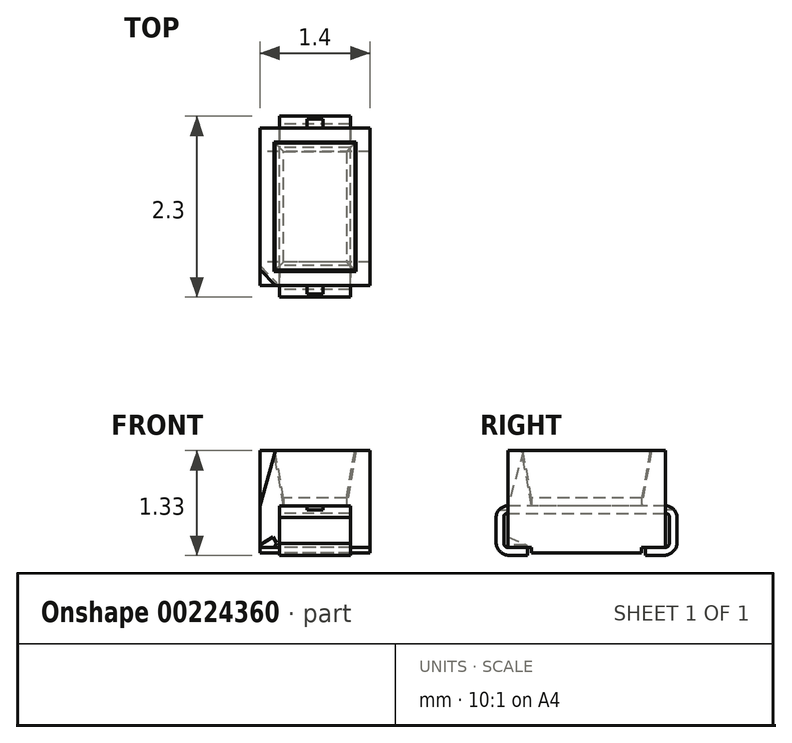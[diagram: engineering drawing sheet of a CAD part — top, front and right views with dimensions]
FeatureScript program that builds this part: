
annotation { "Feature Type Name" : "Feature", "Feature Type Description" : "" }
export const myFeature = defineFeature(function(context is Context, id is Id, definition is map)
    precondition{}
    {
        {
            var Q0;
            Q0=qCreatedBy(makeId("Top.planeOp"),FACE);
            var sketch = newSketch(context, id + "F0", { "sketchPlane" : qUnion([Q0])});
            skLineSegment(sketch, "E0.bottom", {"start": v(0.7, -1) * mm, "end": v(-0.7, -1) * mm});
            skLineSegment(sketch, "E0.top", {"start": v(0.7, 1) * mm, "end": v(-0.7, 1) * mm});
            skLineSegment(sketch, "E0.left", {"start": v(0.7, -1) * mm, "end": v(0.7, 1) * mm});
            skLineSegment(sketch, "E0.right", {"start": v(-0.7, -1) * mm, "end": v(-0.7, 1) * mm});
            skPoint(sketch, "E0.middle", {"position": v(0, 0) * mm});
            skLineSegment(sketch, "E1.bottom", {"start": v(0.4, -0.7) * mm, "end": v(-0.4, -0.7) * mm});
            skLineSegment(sketch, "E1.top", {"start": v(0.4, 0.7) * mm, "end": v(-0.4, 0.7) * mm});
            skLineSegment(sketch, "E1.left", {"start": v(0.4, -0.7) * mm, "end": v(0.4, 0.7) * mm});
            skLineSegment(sketch, "E1.right", {"start": v(-0.4, -0.7) * mm, "end": v(-0.4, 0.7) * mm});
            skLineSegment(sketch, "E2.bottom", {"start": v(0.15, -0.4) * mm, "end": v(-0.15, -0.4) * mm});
            skLineSegment(sketch, "E2.top", {"start": v(0.15, -0.1) * mm, "end": v(-0.15, -0.1) * mm});
            skLineSegment(sketch, "E2.left", {"start": v(0.15, -0.4) * mm, "end": v(0.15, -0.1) * mm});
            skLineSegment(sketch, "E2.right", {"start": v(-0.15, -0.4) * mm, "end": v(-0.15, -0.1) * mm});
            skPoint(sketch, "E2.middle", {"position": v(0, -0.25) * mm});
            skSolve(sketch);
        }
        {
            var Q0;
            Q0=makeQuery(id+"F0.imprint","IMPRINT",FACE,{"disambiguationData":[TD([[makeQuery(id+"F0.imprint","IMPRINT",EDGE,{"derivedFrom":sQuery(id+"F0.wireOp",EDGE,"E0.bottom")}),-1.0]])]});
            var Q1;
            {var subQ1=sQuery(id+"F0.wireOp",EDGE,"E0.top");Q1=makeQuery(id+"F0.imprint","IMPRINT",FACE,{"disambiguationData":[TD([[makeQuery(id+"F0.imprint","IMPRINT",EDGE,{"derivedFrom":subQ1}),1.0]])]});}
            extrude(context, id + "F1", {"entities" : qUnion([Q0, Q1]), "depth" : .7 * mm, "hasSecondDirection" : true, "secondDirectionOppositeDirection" : true, "secondDirectionDepth" : .6 * mm});
        }
        {
            var Q0;
            Q0=makeQuery(id+"F0.imprint","IMPRINT",FACE,{"disambiguationData":[TD([[makeQuery(id+"F0.imprint","IMPRINT",EDGE,{"derivedFrom":sQuery(id+"F0.wireOp",EDGE,"E1.bottom")}),-1.0]])]});
            var Q1;
            Q1=makeQuery(id+"F1.opExtrude","CAP_FACE",FACE,{"disambiguationData":[OSD([sQuery(id+"F0.wireOp",EDGE,"E0.bottom"),sQuery(id+"F0.wireOp",EDGE,"E0.top"),sQuery(id+"F0.wireOp",EDGE,"E0.left"),sQuery(id+"F0.wireOp",EDGE,"E0.right"),sQuery(id+"F0.wireOp",EDGE,"E1.bottom"),sQuery(id+"F0.wireOp",EDGE,"E1.top"),sQuery(id+"F0.wireOp",EDGE,"E1.left"),sQuery(id+"F0.wireOp",EDGE,"E1.right")])],"isStart":false});
            extrude(context, id + "F2", {"entities" : qUnion([Q0]), "operationType" : NewBodyOperationType.REMOVE, "endBound" : BoundingType.UP_TO_SURFACE, "endBoundEntityFace" : qUnion([Q1]), "depth" : 25 * mm, "hasDraft" : true, "draftAngle" : 10 * degree});
        }
        {
            var Q0;
            Q0=makeQuery(id+"F0.imprint","IMPRINT",FACE,{"disambiguationData":[TD([[makeQuery(id+"F0.imprint","IMPRINT",EDGE,{"derivedFrom":sQuery(id+"F0.wireOp",EDGE,"E2.bottom")}),-1.0]])]});
            extrude(context, id + "F3", {"entities" : qUnion([Q0]), "depth" : .1 * mm});
        }
        {
            var Q0;
            Q0=makeQuery(id+"F0.imprint","IMPRINT",FACE,{"disambiguationData":[TD([[makeQuery(id+"F0.imprint","IMPRINT",EDGE,{"derivedFrom":sQuery(id+"F0.wireOp",EDGE,"E1.bottom")}),-1.0]])]});
            var Q1;
            Q1=makeQuery(id+"F1.opExtrude","CAP_FACE",FACE,{"disambiguationData":[OSD([sQuery(id+"F0.wireOp",EDGE,"E0.bottom"),sQuery(id+"F0.wireOp",EDGE,"E0.top"),sQuery(id+"F0.wireOp",EDGE,"E0.left"),sQuery(id+"F0.wireOp",EDGE,"E0.right"),sQuery(id+"F0.wireOp",EDGE,"E1.bottom"),sQuery(id+"F0.wireOp",EDGE,"E1.top"),sQuery(id+"F0.wireOp",EDGE,"E1.left"),sQuery(id+"F0.wireOp",EDGE,"E1.right")])],"isStart":true});
            extrude(context, id + "F4", {"entities" : qUnion([Q0]), "operationType" : NewBodyOperationType.ADD, "endBound" : BoundingType.UP_TO_SURFACE, "oppositeDirection" : true, "endBoundEntityFace" : qUnion([Q1]), "depth" : 25 * mm});
        }
        {
            var Q0;
            Q0=makeQuery(id+"F0.imprint","IMPRINT",FACE,{"disambiguationData":[TD([[makeQuery(id+"F0.imprint","IMPRINT",EDGE,{"derivedFrom":sQuery(id+"F0.wireOp",EDGE,"E1.bottom")}),-1.0]])]});
            extrude(context, id + "F5", {"entities" : qUnion([Q0]), "depth" : .1 * mm});
        }
        {
            var Q0;
            Q0=makeQuery(id+"F0.imprint","IMPRINT",FACE,{"disambiguationData":[TD([[makeQuery(id+"F0.imprint","IMPRINT",EDGE,{"derivedFrom":sQuery(id+"F0.wireOp",EDGE,"E2.bottom")}),-1.0]])]});
            var Q1;
            {var subQ0=sQuery(id+"F0.wireOp",EDGE,"E1.right");var subQ1=sQuery(id+"F0.wireOp",EDGE,"E1.left");var subQ2=sQuery(id+"F0.wireOp",EDGE,"E1.top");var subQ3=sQuery(id+"F0.wireOp",EDGE,"E1.bottom");var subQ4=sQuery(id+"F0.wireOp",EDGE,"E0.right");var subQ5=sQuery(id+"F0.wireOp",EDGE,"E0.left");var subQ6=sQuery(id+"F0.wireOp",EDGE,"E0.top");var subQ7=sQuery(id+"F0.wireOp",EDGE,"E0.bottom");Q1=makeQuery(id+"F4.boolean.opBoolean","MERGE",FACE,{"derivedFrom":[makeQuery(id+"F1.opExtrude","CAP_FACE",FACE,{"disambiguationData":[OSD([subQ7,subQ6,subQ5,subQ4,subQ3,subQ2,subQ1,subQ0])],"isStart":true}),makeQuery(id+"F4.opExtrude","CAP_FACE",FACE,{"disambiguationData":[OSD([subQ7,subQ6,subQ5,subQ4,subQ3,subQ2,subQ1,subQ0])],"isStart":false})]});}
            extrude(context, id + "F6", {"entities" : qUnion([Q0]), "operationType" : NewBodyOperationType.ADD, "endBound" : BoundingType.UP_TO_SURFACE, "oppositeDirection" : true, "endBoundEntityFace" : qUnion([Q1]), "depth" : 25 * mm});
        }
        {
            var Q0;
            Q0=makeQuery(id+"F1.opExtrude","SWEPT_FACE",FACE,{"disambiguationData":[OSD([sQuery(id+"F0.wireOp",EDGE,"E0.right")])]});
            var sketch = newSketch(context, id + "F7", { "sketchPlane" : qUnion([Q0])});
            skLineSegment(sketch, "E3", {"start": v(-1, 0.7) * mm, "end": v(1, 0.7) * mm, "construction": true});
            skLineSegment(sketch, "E4", {"start": v(1, 0.7) * mm, "end": v(1, -0.6) * mm, "construction": true});
            skLineSegment(sketch, "E5", {"start": v(1, -0.6) * mm, "end": v(-1, -0.6) * mm, "construction": true});
            skLineSegment(sketch, "E6", {"start": v(-1, -0.6) * mm, "end": v(-1, 0.7) * mm, "construction": true});
            skLineSegment(sketch, "E7", {"start": v(-1.16, -0.53) * mm, "end": v(-0.7, -0.53) * mm});
            skLineSegment(sketch, "E8", {"start": v(-0.7, -0.53) * mm, "end": v(-0.7, -0.74) * mm});
            skLineSegment(sketch, "E9", {"start": v(-0.7, -0.74) * mm, "end": v(0.7, -0.74) * mm});
            skLineSegment(sketch, "E10", {"start": v(0.7, -0.74) * mm, "end": v(0.7, -0.53) * mm});
            skLineSegment(sketch, "E11", {"start": v(0.7, -0.53) * mm, "end": v(1.16, -0.53) * mm});
            skLineSegment(sketch, "E12", {"start": v(1.16, -0.53) * mm, "end": v(1.16, -0.97) * mm});
            skLineSegment(sketch, "E13", {"start": v(1.16, -0.97) * mm, "end": v(-1.16, -0.97) * mm});
            skLineSegment(sketch, "E14", {"start": v(-1.16, -0.97) * mm, "end": v(-1.16, -0.53) * mm});
            skSolve(sketch);
        }
        {
            var Q0;
            {var subQ0=sQuery(id+"F7.wireOp",EDGE,"E8");var subQ1=sQuery(id+"F7.wireOp",EDGE,"E7");var subQ2=makeQuery(id+"F7.imprint","INTERSECT",VERTEX,{"derivedFrom":[subQ1,subQ0]});Q0=makeQuery(id+"F7.imprint","IMPRINT",FACE,{"disambiguationData":[TD([[makeQuery(id+"F7.imprint","IMPRINT",EDGE,{"disambiguationData":[TD([[subQ2,-1.0]])],"derivedFrom":subQ0}),-1.0]])]});}
            var Q1;
            {var subQ0=sQuery(id+"F7.wireOp",EDGE,"E11");var subQ1=sQuery(id+"F7.wireOp",EDGE,"E10");var subQ2=makeQuery(id+"F7.imprint","INTERSECT",VERTEX,{"derivedFrom":[subQ1,subQ0]});Q1=makeQuery(id+"F7.imprint","IMPRINT",FACE,{"disambiguationData":[TD([[makeQuery(id+"F7.imprint","IMPRINT",EDGE,{"disambiguationData":[TD([[subQ2,1.0]])],"derivedFrom":subQ1}),-1.0]])]});}
            extrude(context, id + "F8", {"entities" : qUnion([Q0, Q1]), "operationType" : NewBodyOperationType.REMOVE, "endBound" : BoundingType.UP_TO_NEXT, "oppositeDirection" : true, "depth" : 25 * mm});
        }
        {
            var Q0;
            Q0=makeQuery(id+"F1.opExtrude","SWEPT_FACE",FACE,{"disambiguationData":[OSD([sQuery(id+"F0.wireOp",EDGE,"E0.right")])]});
            var sketch = newSketch(context, id + "F9", { "sketchPlane" : qUnion([Q0])});
            skLineSegment(sketch, "E15", {"start": v(-1, 0) * mm, "end": v(1, 0) * mm, "construction": true});
            skLineSegment(sketch, "E16", {"start": v(-1.15, -0.15) * mm, "end": v(-1.15, -0.48) * mm});
            skLineSegment(sketch, "E17", {"start": v(-1, -0.63) * mm, "end": v(-0.75, -0.63) * mm});
            skLineSegment(sketch, "E18", {"start": v(-1.15, 0) * mm, "end": v(1.15, 0) * mm});
            skLineSegment(sketch, "E19", {"start": v(1.15, -0.15) * mm, "end": v(1.15, -0.48) * mm});
            skLineSegment(sketch, "E20", {"start": v(1, -0.63) * mm, "end": v(0.75, -0.63) * mm});
            skLineSegment(sketch, "E21", {"start": v(0.75, -0.63) * mm, "end": v(0.75, -0.53) * mm});
            skLineSegment(sketch, "E22", {"start": v(0.75, -0.53) * mm, "end": v(1, -0.53) * mm});
            skLineSegment(sketch, "E23", {"start": v(1.05, -0.48) * mm, "end": v(1.05, -0.15) * mm});
            skLineSegment(sketch, "E24", {"start": v(1, -0.1) * mm, "end": v(-1, -0.1) * mm});
            skLineSegment(sketch, "E25", {"start": v(-1.05, -0.15) * mm, "end": v(-1.05, -0.48) * mm});
            skLineSegment(sketch, "E26", {"start": v(-1, -0.53) * mm, "end": v(-0.75, -0.53) * mm});
            skLineSegment(sketch, "E27", {"start": v(-0.75, -0.53) * mm, "end": v(-0.75, -0.63) * mm});
            skPoint(sketch, "E28.visualSharp", {"position": v(-1.05, -0.1) * mm});
            skArc(sketch, "E28.filletArc", {"start": v(-1, -0.1) * mm, "mid": v(-1.04, -0.11) * mm, "end": v(-1.05, -0.15) * mm});
            skPoint(sketch, "E29.newPointA", {"position": v(0, 0) * mm});
            skArc(sketch, "E29.filletArc", {"start": v(-1, 0) * mm, "mid": v(-1.1, -0.04) * mm, "end": v(-1.15, -0.15) * mm});
            skPoint(sketch, "E30.visualSharp", {"position": v(-1.15, -0.63) * mm});
            skArc(sketch, "E30.filletArc", {"start": v(-1.15, -0.48) * mm, "mid": v(-1.1, -0.58) * mm, "end": v(-1, -0.63) * mm});
            skPoint(sketch, "E31.visualSharp", {"position": v(-1.05, -0.53) * mm});
            skArc(sketch, "E31.filletArc", {"start": v(-1.05, -0.48) * mm, "mid": v(-1.04, -0.51) * mm, "end": v(-1, -0.53) * mm});
            skPoint(sketch, "E32.visualSharp", {"position": v(1.05, -0.53) * mm});
            skArc(sketch, "E32.filletArc", {"start": v(1, -0.53) * mm, "mid": v(1.04, -0.51) * mm, "end": v(1.05, -0.48) * mm});
            skPoint(sketch, "E33.visualSharp", {"position": v(1.05, -0.1) * mm});
            skArc(sketch, "E33.filletArc", {"start": v(1.05, -0.15) * mm, "mid": v(1.04, -0.11) * mm, "end": v(1, -0.1) * mm});
            skArc(sketch, "E34.filletArc", {"start": v(1.15, -0.15) * mm, "mid": v(1.1, -0.04) * mm, "end": v(1, 0) * mm});
            skPoint(sketch, "E35.visualSharp", {"position": v(1.15, -0.63) * mm});
            skArc(sketch, "E35.filletArc", {"start": v(1, -0.63) * mm, "mid": v(1.1, -0.58) * mm, "end": v(1.15, -0.48) * mm});
            skSolve(sketch);
        }
        {
            var Q0;
            Q0=qSketchRegion(id+"F9",true);
            var Q1;
            Q1=makeQuery(id+"F1.opExtrude","SWEPT_FACE",FACE,{"disambiguationData":[OSD([sQuery(id+"F0.wireOp",EDGE,"E0.left")])]});
            extrude(context, id + "F10", {"entities" : qUnion([Q0]), "oppositeDirection" : true, "endBoundEntityFace" : qUnion([Q1]), "depth" : 1.15 * mm, "hasSecondDirection" : true, "secondDirectionOppositeDirection" : true, "secondDirectionDepth" : .25 * mm});
        }
        {
            var Q0;
            Q0=makeQuery(id+"F5.opExtrude","CAP_FACE",FACE,{"disambiguationData":[OSD([sQuery(id+"F0.wireOp",EDGE,"E1.bottom"),sQuery(id+"F0.wireOp",EDGE,"E1.top"),sQuery(id+"F0.wireOp",EDGE,"E1.left"),sQuery(id+"F0.wireOp",EDGE,"E1.right"),sQuery(id+"F0.wireOp",EDGE,"E2.bottom"),sQuery(id+"F0.wireOp",EDGE,"E2.top"),sQuery(id+"F0.wireOp",EDGE,"E2.left"),sQuery(id+"F0.wireOp",EDGE,"E2.right")])],"isStart":false});
            var sketch = newSketch(context, id + "F11", { "sketchPlane" : qUnion([Q0])});
            skLineSegment(sketch, "E36.0.1", {"start": v(-0.45, 1) * mm, "end": v(0.45, 1) * mm});
            skLineSegment(sketch, "E37", {"start": v(0, 1) * mm, "end": v(0.1, 1) * mm});
            skLineSegment(sketch, "E38", {"start": v(0.1, 1) * mm, "end": v(0.1, 1.2) * mm});
            skLineSegment(sketch, "E39", {"start": v(0.1, 1.2) * mm, "end": v(-0.1, 1.2) * mm});
            skLineSegment(sketch, "E40", {"start": v(-0.1, 1.2) * mm, "end": v(-0.1, 1) * mm});
            skLineSegment(sketch, "E41", {"start": v(-0.1, 1) * mm, "end": v(0, 1) * mm});
            skPoint(sketch, "E42.startSnap0", {"position": v(-0.15, -0.25) * mm});
            skPoint(sketch, "E36.0.2.end.orphan", {"position": v(0.45, 1.15) * mm});
            skPoint(sketch, "E36.0.0.start.orphan", {"position": v(-0.45, 1.15) * mm});
            skLineSegment(sketch, "E43", {"start": v(-0.78, 0) * mm, "end": v(1.2, 0) * mm, "construction": true});
            skLineSegment(sketch, "E44.MirrorCS", {"start": v(-0.1, -1) * mm, "end": v(0, -1) * mm});
            skLineSegment(sketch, "E45.MirrorCS", {"start": v(-0.1, -1.2) * mm, "end": v(-0.1, -1) * mm});
            skLineSegment(sketch, "E46.MirrorCS", {"start": v(0, -1) * mm, "end": v(0.1, -1) * mm});
            skLineSegment(sketch, "E47.MirrorCS", {"start": v(0.1, -1.2) * mm, "end": v(-0.1, -1.2) * mm});
            skLineSegment(sketch, "E48.MirrorCS", {"start": v(0.1, -1) * mm, "end": v(0.1, -1.2) * mm});
            skSolve(sketch);
        }
        {
            var Q0;
            Q0=qSketchRegion(id+"F11",true);
            extrude(context, id + "F12", {"entities" : qUnion([Q0]), "operationType" : NewBodyOperationType.REMOVE, "oppositeDirection" : true, "depth" : .15 * mm});
        }
        {
            var Q0;
            Q0=makeQuery(id+"F1.opExtrude","SWEPT_FACE",FACE,{"disambiguationData":[OSD([sQuery(id+"F0.wireOp",EDGE,"E0.bottom")])]});
            var sketch = newSketch(context, id + "F13", { "sketchPlane" : qUnion([Q0])});
            skLineSegment(sketch, "E49", {"start": v(-0.7, 0) * mm, "end": v(-0.5, 0.7) * mm});
            skLineSegment(sketch, "E50", {"start": v(-0.7, -0.13) * mm, "end": v(-0.45, -0.53) * mm});
            skSolve(sketch);
        }
        {
            var Q0;
            Q0=makeQuery(id+"F1.opExtrude","SWEPT_FACE",FACE,{"disambiguationData":[OSD([sQuery(id+"F0.wireOp",EDGE,"E0.right")])]});
            var sketch = newSketch(context, id + "F14", { "sketchPlane" : qUnion([Q0])});
            skLineSegment(sketch, "E51", {"start": v(0.8, 0.7) * mm, "end": v(1, 0) * mm});
            skLineSegment(sketch, "E52", {"start": v(1, 0) * mm, "end": v(1, 0.7) * mm});
            skLineSegment(sketch, "E53", {"start": v(0.7, -0.53) * mm, "end": v(1, -0.53) * mm});
            skLineSegment(sketch, "E54", {"start": v(1, 0.7) * mm, "end": v(1, -0.53) * mm});
            skLineSegment(sketch, "E55", {"start": v(1, 0.7) * mm, "end": v(-1, 0.7) * mm});
            skLineSegment(sketch, "E56", {"start": v(-1, 0.7) * mm, "end": v(-1, -0.53) * mm});
            skLineSegment(sketch, "E57", {"start": v(-1, -0.53) * mm, "end": v(-0.7, -0.53) * mm});
            skLineSegment(sketch, "E58", {"start": v(-0.7, -0.53) * mm, "end": v(-0.7, -0.6) * mm});
            skLineSegment(sketch, "E59", {"start": v(0.7, -0.6) * mm, "end": v(-0.7, -0.6) * mm});
            skLineSegment(sketch, "E60", {"start": v(0.7, -0.6) * mm, "end": v(0.7, -0.53) * mm});
            skLineSegment(sketch, "E61", {"start": v(1, -0.13) * mm, "end": v(0.75, -0.53) * mm});
            skSolve(sketch);
        }
        {
            var Q0;
            Q0=makeQuery(id+"F1.opExtrude","CAP_FACE",FACE,{"disambiguationData":[OSD([sQuery(id+"F0.wireOp",EDGE,"E0.bottom"),sQuery(id+"F0.wireOp",EDGE,"E0.top"),sQuery(id+"F0.wireOp",EDGE,"E0.left"),sQuery(id+"F0.wireOp",EDGE,"E0.right"),sQuery(id+"F0.wireOp",EDGE,"E1.bottom"),sQuery(id+"F0.wireOp",EDGE,"E1.top"),sQuery(id+"F0.wireOp",EDGE,"E1.left"),sQuery(id+"F0.wireOp",EDGE,"E1.right")])],"isStart":false});
            var sketch = newSketch(context, id + "F15", { "sketchPlane" : qUnion([Q0])});
            skLineSegment(sketch, "E62", {"start": v(-0.7, -0.8) * mm, "end": v(-0.5, -1) * mm});
            skSolve(sketch);
        }
        {
            var Q0;
            Q0=sQuery(id+"F15.wireOp",VERTEX,"E62.start");
            var Q1;
            Q1=sQuery(id+"F15.wireOp",VERTEX,"E62.end");
            var Q2;
            Q2=sQuery(id+"F14.wireOp",VERTEX,"E52.start");
            cPlane(context, id + "F16", {"entities" : qUnion([Q0, Q1, Q2]), "cplaneType" : CPlaneType.THREE_POINT, "offset" : 25 * mm, "width" : 150 * mm, "height" : 150 * mm});
        }
        {
            var Q0;
            Q0=qCreatedBy(id+"F16.planeOp",FACE);
            var sketch = newSketch(context, id + "F17", { "sketchPlane" : qUnion([Q0])});
            skLineSegment(sketch, "E63.bottom", {"start": v(-0.04, 0.54) * mm, "end": v(0.57, 0.54) * mm});
            skLineSegment(sketch, "E63.top", {"start": v(-0.04, -0.39) * mm, "end": v(0.57, -0.39) * mm});
            skLineSegment(sketch, "E63.left", {"start": v(-0.04, 0.54) * mm, "end": v(-0.04, -0.39) * mm});
            skLineSegment(sketch, "E63.right", {"start": v(0.57, 0.54) * mm, "end": v(0.57, -0.39) * mm});
            skSolve(sketch);
        }
        {
            var Q0;
            Q0=qSketchRegion(id+"F17",true);
            extrude(context, id + "F18", {"entities" : qUnion([Q0]), "operationType" : NewBodyOperationType.REMOVE, "endBound" : BoundingType.UP_TO_NEXT, "depth" : 25 * mm});
        }
        {
            var Q0;
            Q0=makeQuery(id+"F8.boolean.opBoolean","COPY",FACE,{"derivedFrom":makeQuery(id+"F8.opExtrude","SWEPT_FACE",FACE,{"disambiguationData":[OSD([sQuery(id+"F7.wireOp",EDGE,"E11")])]})});
            var sketch = newSketch(context, id + "F19", { "sketchPlane" : qUnion([Q0])});
            skLineSegment(sketch, "E64", {"start": v(-0.7, 0.75) * mm, "end": v(-0.45, 1) * mm});
            skSolve(sketch);
        }
        {
            var Q0;
            Q0=sQuery(id+"F14.wireOp",VERTEX,"E61.start");
            var Q1;
            Q1=sQuery(id+"F19.wireOp",VERTEX,"E64.start");
            var Q2;
            Q2=sQuery(id+"F19.wireOp",VERTEX,"E64.end");
            cPlane(context, id + "F20", {"entities" : qUnion([Q0, Q1, Q2]), "cplaneType" : CPlaneType.THREE_POINT, "offset" : 25 * mm, "width" : 150 * mm, "height" : 150 * mm});
        }
        {
            var Q0;
            Q0=qCreatedBy(id+"F20.planeOp",FACE);
            var sketch = newSketch(context, id + "F21", { "sketchPlane" : qUnion([Q0])});
            skLineSegment(sketch, "E65.0", {"start": v(-0.34, 0.26) * mm, "end": v(0, -0.07) * mm});
            skLineSegment(sketch, "E65.1", {"start": v(-0.34, 0.26) * mm, "end": v(-0.34, -0.2) * mm});
            skLineSegment(sketch, "E65.2", {"start": v(0, -0.07) * mm, "end": v(-0.34, -0.2) * mm});
            skSolve(sketch);
        }
        {
            var Q0;
            Q0 = qSketchRegion(id + "F21", true);
            extrude(context, id + "F22", {"entities" : qUnion([Q0]), "operationType" : NewBodyOperationType.REMOVE, "endBound" : BoundingType.THROUGH_ALL, "oppositeDirection" : true, "depth" : 25 * mm});
        }
        {
            var Q0;
            Q0=makeQuery(id+"F5.opExtrude","CAP_FACE",FACE,{"disambiguationData":[OSD([sQuery(id+"F0.wireOp",EDGE,"E1.bottom"),sQuery(id+"F0.wireOp",EDGE,"E1.top"),sQuery(id+"F0.wireOp",EDGE,"E1.left"),sQuery(id+"F0.wireOp",EDGE,"E1.right"),sQuery(id+"F0.wireOp",EDGE,"E2.bottom"),sQuery(id+"F0.wireOp",EDGE,"E2.top"),sQuery(id+"F0.wireOp",EDGE,"E2.left"),sQuery(id+"F0.wireOp",EDGE,"E2.right")])],"isStart":false});
            var sketch = newSketch(context, id + "F23", { "sketchPlane" : qUnion([Q0])});
            skLineSegment(sketch, "E66", {"start": v(-0.4, 0.7) * mm, "end": v(-0.4, -0.7) * mm});
            skLineSegment(sketch, "E67", {"start": v(-0.4, -0.7) * mm, "end": v(0.4, -0.7) * mm});
            skLineSegment(sketch, "E68", {"start": v(0.4, -0.7) * mm, "end": v(0.4, 0.7) * mm});
            skLineSegment(sketch, "E69", {"start": v(0.4, 0.7) * mm, "end": v(-0.4, 0.7) * mm});
            skSolve(sketch);
        }
        {
            var Q0;
            Q0 = qSketchRegion(id + "F23", true);
            var Q1;
            Q1=makeQuery(id+"F1.opExtrude","CAP_FACE",FACE,{"disambiguationData":[OSD([sQuery(id+"F0.wireOp",EDGE,"E0.bottom"),sQuery(id+"F0.wireOp",EDGE,"E0.top"),sQuery(id+"F0.wireOp",EDGE,"E0.left"),sQuery(id+"F0.wireOp",EDGE,"E0.right"),sQuery(id+"F0.wireOp",EDGE,"E1.bottom"),sQuery(id+"F0.wireOp",EDGE,"E1.top"),sQuery(id+"F0.wireOp",EDGE,"E1.left"),sQuery(id+"F0.wireOp",EDGE,"E1.right")])],"isStart":false});
            extrude(context, id + "F24", {"entities" : qUnion([Q0]), "endBound" : BoundingType.UP_TO_SURFACE, "endBoundEntityFace" : qUnion([Q1]), "depth" : 25 * mm, "hasDraft" : true, "draftAngle" : 10 * degree});
        }
    });
